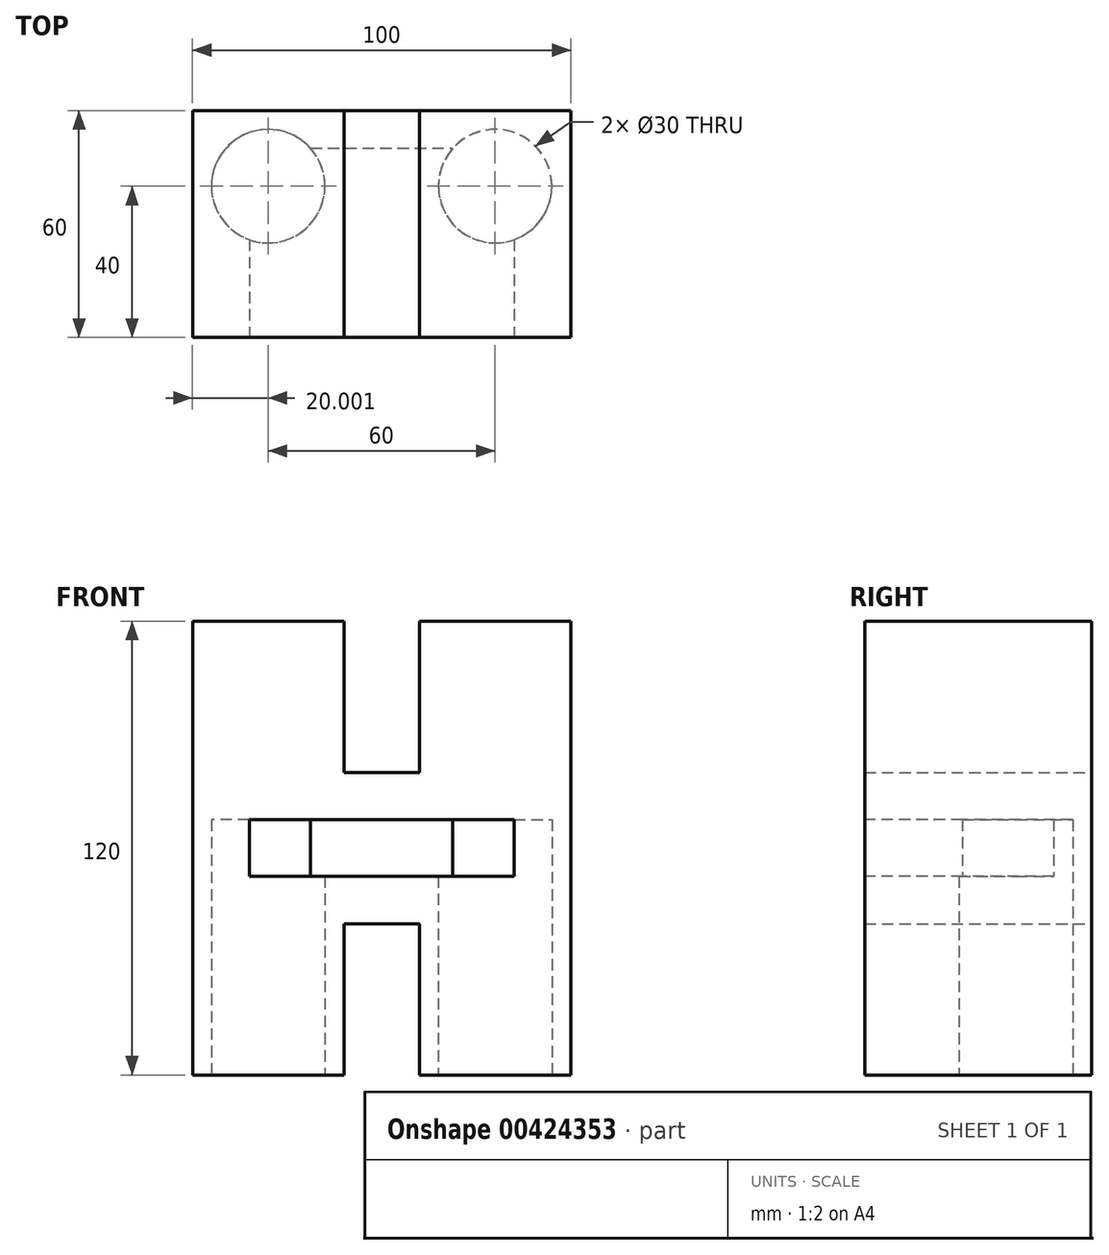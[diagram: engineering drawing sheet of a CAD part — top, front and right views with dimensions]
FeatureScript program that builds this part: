
annotation { "Feature Type Name" : "Feature", "Feature Type Description" : "" }
export const myFeature = defineFeature(function(context is Context, id is Id, definition is map)
    precondition{}
    {
        {
            var Q0;
            Q0=qCreatedBy(makeId("Front.planeOp"),FACE);
            var sketch = newSketch(context, id + "F0", { "sketchPlane" : qUnion([Q0])});
            skLineSegment(sketch, "E0.bottom", {"start": v(-48.04, 59.25) * mm, "end": v(-8.04, 59.25) * mm});
            skLineSegment(sketch, "E0.top", {"start": v(-48.04, -60.75) * mm, "end": v(-8.04, -60.75) * mm});
            skLineSegment(sketch, "E0.left", {"start": v(-48.04, 59.25) * mm, "end": v(-48.04, -60.75) * mm});
            skLineSegment(sketch, "E0.right", {"start": v(51.96, 59.25) * mm, "end": v(51.96, -60.75) * mm});
            skLineSegment(sketch, "E1", {"start": v(-8.04, 59.25) * mm, "end": v(-8.04, 19.25) * mm});
            skLineSegment(sketch, "E2", {"start": v(-8.04, 19.25) * mm, "end": v(11.96, 19.25) * mm});
            skLineSegment(sketch, "E3", {"start": v(11.96, 19.25) * mm, "end": v(11.96, 59.25) * mm});
            skLineSegment(sketch, "E4", {"start": v(11.96, -60.75) * mm, "end": v(11.96, -20.75) * mm});
            skLineSegment(sketch, "E5", {"start": v(11.96, -20.75) * mm, "end": v(-8.04, -20.75) * mm});
            skLineSegment(sketch, "E6", {"start": v(-8.04, -20.75) * mm, "end": v(-8.04, -60.75) * mm});
            skLineSegment(sketch, "E7.trimOffspring", {"start": v(11.96, -60.75) * mm, "end": v(51.96, -60.75) * mm});
            skLineSegment(sketch, "E8.trimOffspring", {"start": v(11.96, 59.25) * mm, "end": v(51.96, 59.25) * mm});
            skSolve(sketch);
        }
        {
            var Q0;
            Q0=makeQuery(id+"F0.imprint","IMPRINT",FACE,{"disambiguationData":[TD([[makeQuery(id+"F0.imprint","IMPRINT",EDGE,{"derivedFrom":sQuery(id+"F0.wireOp",EDGE,"E0.bottom")}),-1.0]])]});
            extrude(context, id + "F1", {"entities" : qUnion([Q0]), "depth" : 60 * mm});
        }
        {
            var Q0;
            Q0=makeQuery(id+"F1.opExtrude","CAP_FACE",FACE,{"disambiguationData":[OSD([sQuery(id+"F0.wireOp",EDGE,"E0.bottom"),sQuery(id+"F0.wireOp",EDGE,"E0.top"),sQuery(id+"F0.wireOp",EDGE,"E0.left"),sQuery(id+"F0.wireOp",EDGE,"E0.right"),sQuery(id+"F0.wireOp",EDGE,"E1"),sQuery(id+"F0.wireOp",EDGE,"E2"),sQuery(id+"F0.wireOp",EDGE,"E3"),sQuery(id+"F0.wireOp",EDGE,"E4"),sQuery(id+"F0.wireOp",EDGE,"E5"),sQuery(id+"F0.wireOp",EDGE,"E6"),sQuery(id+"F0.wireOp",EDGE,"E7.trimOffspring"),sQuery(id+"F0.wireOp",EDGE,"E8.trimOffspring")])],"isStart":false});
            var sketch = newSketch(context, id + "F2", { "sketchPlane" : qUnion([Q0])});
            skLineSegment(sketch, "E9.bottom", {"start": v(-33.04, 6.75) * mm, "end": v(36.96, 6.75) * mm});
            skLineSegment(sketch, "E9.top", {"start": v(-33.04, -8.25) * mm, "end": v(36.96, -8.25) * mm});
            skLineSegment(sketch, "E9.left", {"start": v(-33.04, 6.75) * mm, "end": v(-33.04, -8.25) * mm});
            skLineSegment(sketch, "E9.right", {"start": v(36.96, 6.75) * mm, "end": v(36.96, -8.25) * mm});
            skSolve(sketch);
        }
        {
            var Q0;
            Q0=makeQuery(id+"F2.imprint","IMPRINT",FACE,{"disambiguationData":[TD([[makeQuery(id+"F2.imprint","IMPRINT",EDGE,{"derivedFrom":sQuery(id+"F2.wireOp",EDGE,"E9.bottom")}),-1.0]])]});
            extrude(context, id + "F3", {"entities" : qUnion([Q0]), "operationType" : NewBodyOperationType.REMOVE, "oppositeDirection" : true, "depth" : 50 * mm});
        }
        {
            var Q0;
            Q0=makeQuery(id+"F1.opExtrude","SWEPT_FACE",FACE,{"disambiguationData":[OSD([sQuery(id+"F0.wireOp",EDGE,"E0.top")])]});
            var sketch = newSketch(context, id + "F4", { "sketchPlane" : qUnion([Q0])});
            skCircle(sketch, "E10", {"center": v(-28.04, 20) * mm, "radius": 15 * mm});
            skSolve(sketch);
        }
        {
            var Q0;
            Q0=makeQuery(id+"F1.opExtrude","SWEPT_FACE",FACE,{"disambiguationData":[OSD([sQuery(id+"F0.wireOp",EDGE,"E7.trimOffspring")])]});
            var sketch = newSketch(context, id + "F5", { "sketchPlane" : qUnion([Q0])});
            skCircle(sketch, "E11", {"center": v(31.96, 20) * mm, "radius": 15 * mm});
            skSolve(sketch);
        }
        {
            var Q0;
            Q0=makeQuery(id+"F4.imprint","IMPRINT",FACE,{"disambiguationData":[TD([[makeQuery(id+"F4.imprint","IMPRINT",EDGE,{"derivedFrom":sQuery(id+"F4.wireOp",EDGE,"E10")}),1.0]])]});
            var Q1;
            Q1=makeQuery(id+"F5.imprint","IMPRINT",FACE,{"disambiguationData":[TD([[makeQuery(id+"F5.imprint","IMPRINT",EDGE,{"derivedFrom":sQuery(id+"F5.wireOp",EDGE,"E11")}),1.0]])]});
            var Q2;
            Q2=sQuery(id+"F4.wireOp",EDGE,"E10");
            extrude(context, id + "F6", {"entities" : qUnion([Q0, Q1]), "operationType" : NewBodyOperationType.REMOVE, "surfaceEntities" : qUnion([Q2]), "oppositeDirection" : true, "depth" : 67.5 * mm});
        }
    });
